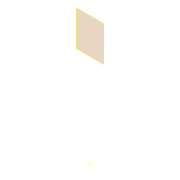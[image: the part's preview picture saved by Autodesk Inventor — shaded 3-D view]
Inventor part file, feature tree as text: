
AUTODESK INVENTOR PART (.ipt)
format: ipt  version: 2022 (Build 260153000, 153)  size: 73,728 bytes
history: native  units: mm
features: reference x10, other x6, plane x2, sketch x1
ambient origin geometry x8: Origin, YZ Plane, XZ Plane, XY Plane, X Axis, Y Axis, Z Axis, Center Point
feature tree (19):
  plane  "Arbeitsebene1"
  plane  "Arbeitsebene2"
  sketch  "Skizze2"  dims[d0=7.3mm d1=7.2mm d2=7.2mm d3=7.2mm]
  reference  "Referenz1"
  reference  "Referenz2"
  reference  "Referenz3"
  reference  "Referenz4"
  reference  "Referenz5"
  reference  "Referenz6"
  reference  "Referenz7"
  reference  "Referenz8"
  reference  "Referenz9"
  reference  "Referenz10"
  other  "Omnicscope_Xiao.iam"
  other  "00_Seeeduino Xiao:1"
  other  "00_Seeeduino Xiao:7"
  other  "00_Seeeduino Xiao:13"
  other  "Omniscope_USBC_Bar:1"
  other  "00_Seeeduino Xiao:19"
